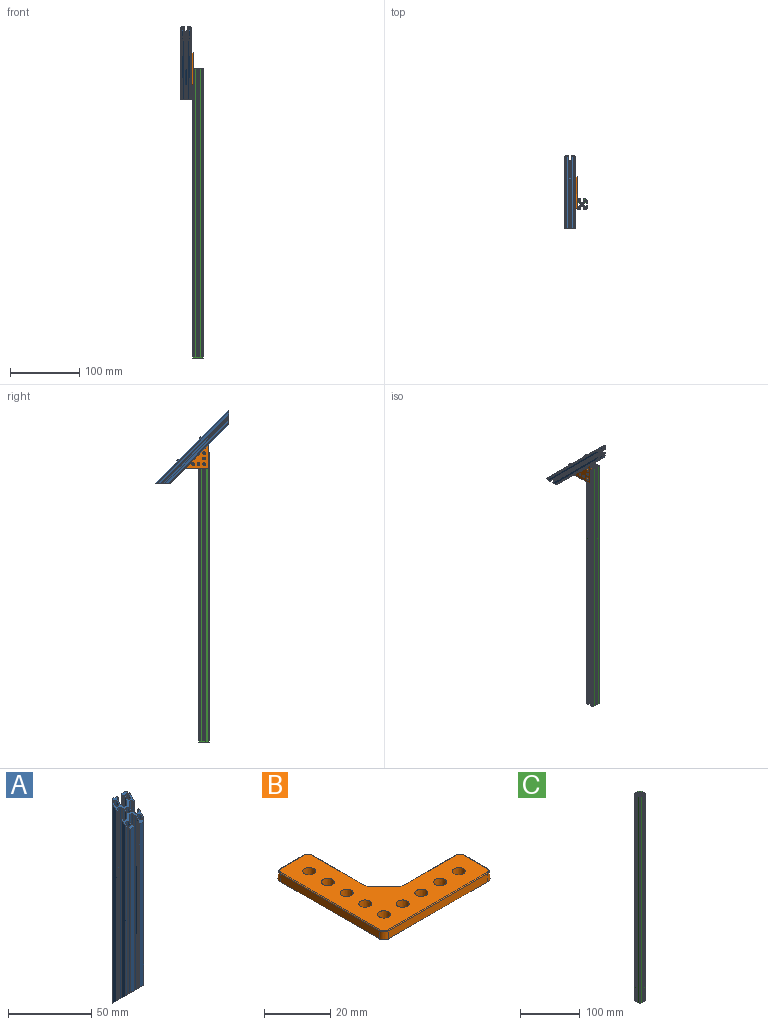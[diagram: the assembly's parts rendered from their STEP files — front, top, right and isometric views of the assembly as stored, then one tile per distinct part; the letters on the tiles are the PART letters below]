
ASSEMBLY  parts=3 mates=2
PART A: 115 faces, bbox 15x15x150 mm
  f0: plane 15x15mm, normal (0,-0.71,0.71), area 128.4mm2, adj f2,f3,f4,f5,f6,f7,f8,f9
  f1: plane 15x15mm, normal (0,-0.71,-0.71), area 128.4mm2, adj f2,f3,f4,f5,f6,f7,f8,f9
  f2: cylinder r=0.5mm len=130.3mm, axis (0,0,1), area 101.8mm2, adj f0,f1,f3,f4
  f3: plane 129.3x2.1mm, normal (0,1,0), area 271.5mm2, adj f0,f1,f2,f63
  f4: plane 130.8x0.25mm, normal (-1,0,0), area 32.6mm2, adj f0,f1,f2,f5
  f5: cylinder r=0.5mm len=131.8mm, axis (0,0,-1), area 103.2mm2, adj f0,f1,f4,f6
  f6: cylinder r=1mm len=133.8mm, axis (0,0,1), area 208.2mm2, adj f0,f1,f5,f7
  f7: plane 136.2x1.2mm, normal (-1,0,0), area 162mm2, adj f0,f1,f6,f8
  f8: cylinder r=1mm len=138.2mm, axis (0,0,1), area 215.9mm2, adj f0,f1,f7,f9
  f9: cylinder r=0.5mm len=139.2mm, axis (0,0,-1), area 108.8mm2, adj f0,f1,f8,f10
  f10: plane 139.7x0.25mm, normal (-1,0,0), area 34.9mm2, adj f0,f1,f9,f11
  f11: cylinder r=0.5mm len=140.7mm, axis (0,0,1), area 110.2mm2, adj f0,f1,f10,f12
  f12: plane 140.7x2.1mm, normal (0,-1,0), area 295.5mm2, adj f0,f1,f11,f13
  f13: cylinder r=0.2mm len=140.7mm, axis (0,0,1), area 44.2mm2, adj f0,f1,f12,f14
  f14: plane 140.3x0.4mm, normal (1,0,0), area 56mm2, adj f0,f1,f13,f15
  f15: cylinder r=0.5mm len=139.5mm, axis (0,0,-1), area 109.1mm2, adj f0,f1,f14,f16
  f16: plane 138.5x0.2mm, normal (0,-1,0), area 27.7mm2, adj f0,f1,f15,f17
  f17: cylinder r=0.5mm len=139.5mm, axis (0,0,-1), area 109.1mm2, adj f0,f1,f16,f18
  f18: plane 146.17x3.34mm, normal (-1,0,0), area 476.5mm2, adj f0,f1,f17,f19
  f19: cylinder r=0.5mm len=147.17mm, axis (0,0,-1), area 173.1mm2, adj f0,f1,f18,f20
  f20: plane 146.88x0.48mm, normal (0.71,0.71,0), area 100mm2, adj f0,f1,f19,f21
  f21: cylinder r=1.25mm len=147.51mm, axis (0,0,-1), area 987.9mm2, adj f0,f1,f20,f22
  f22: plane 148.29x0.48mm, normal (-0.71,-0.71,0), area 100.9mm2, adj f0,f1,f21,f23
  f23: cylinder r=0.5mm len=150mm, axis (0,0,1), area 175.9mm2, adj f0,f1,f22,f64
  f24: cylinder r=0.5mm len=150mm, axis (0,0,-1), area 117.5mm2, adj f0,f1,f25,f64
  f25: plane 149x0.2mm, normal (1,0,0), area 29.8mm2, adj f0,f1,f24,f26
  f26: cylinder r=0.5mm len=148.6mm, axis (0,0,-1), area 116.2mm2, adj f0,f1,f25,f27
  f27: plane 147.6x0.4mm, normal (0,-1,0), area 59mm2, adj f0,f1,f26,f28
  f28: cylinder r=0.2mm len=147.6mm, axis (0,0,1), area 46.3mm2, adj f0,f1,f27,f29
  f29: plane 147.2x2.1mm, normal (1,0,0), area 304.7mm2, adj f0,f1,f28,f30
  f30: cylinder r=0.5mm len=143mm, axis (0,0,1), area 111.8mm2, adj f0,f1,f29,f31
  f31: plane 142x0.25mm, normal (0,1,0), area 35.5mm2, adj f0,f1,f30,f32
  f32: cylinder r=0.5mm len=142mm, axis (0,0,-1), area 111.2mm2, adj f0,f1,f31,f33
  f33: cylinder r=1mm len=141mm, axis (0,0,1), area 219.5mm2, adj f0,f1,f32,f34
  f34: plane 139x1.2mm, normal (0,1,0), area 166.8mm2, adj f0,f1,f33,f35
  f35: cylinder r=1mm len=141mm, axis (0,0,1), area 219.5mm2, adj f0,f1,f34,f36
  f36: cylinder r=0.5mm len=142mm, axis (0,0,-1), area 111.2mm2, adj f0,f1,f35,f37
  f37: plane 142x0.25mm, normal (0,1,0), area 35.5mm2, adj f0,f1,f36,f38
  f38: cylinder r=0.5mm len=143mm, axis (0,0,1), area 111.8mm2, adj f0,f1,f37,f39
  f39: plane 147.2x2.1mm, normal (-1,0,0), area 304.7mm2, adj f0,f1,f38,f40
  f40: cylinder r=0.2mm len=147.6mm, axis (0,0,1), area 46.3mm2, adj f0,f1,f39,f41
  f41: plane 147.6x0.4mm, normal (0,-1,0), area 59mm2, adj f0,f1,f40,f42
  f42: cylinder r=0.5mm len=148.6mm, axis (0,0,-1), area 116.2mm2, adj f0,f1,f41,f44
  f43: cylinder r=0.5mm len=131.5mm, axis (0,0,-1), area 103mm2, adj f0,f1,f45,f71
  f44: plane 149x0.2mm, normal (-1,0,0), area 29.8mm2, adj f0,f1,f42,f46
  f45: plane 131.5x0.2mm, normal (0,1,0), area 26.3mm2, adj f0,f1,f43,f47
  f46: cylinder r=0.5mm len=150mm, axis (0,0,-1), area 117.5mm2, adj f0,f1,f44,f65
  f47: cylinder r=0.5mm len=131.5mm, axis (0,0,-1), area 103mm2, adj f0,f1,f45,f48
  f48: plane 130.5x0.4mm, normal (-1,0,0), area 52mm2, adj f0,f1,f47,f50
  f49: cylinder r=0.5mm len=150mm, axis (0,0,-1), area 175.9mm2, adj f0,f1,f51,f65
  f50: cylinder r=0.2mm len=129.7mm, axis (0,0,1), area 40.7mm2, adj f0,f1,f48,f86
  f51: plane 148.29x0.48mm, normal (0.71,-0.71,0), area 100.9mm2, adj f0,f1,f49,f52
  f52: cylinder r=1.25mm len=147.51mm, axis (0,0,-1), area 987.9mm2, adj f0,f1,f51,f53
  f53: plane 146.88x0.48mm, normal (-0.71,0.71,0), area 100mm2, adj f0,f1,f52,f54
  f54: cylinder r=0.5mm len=147.17mm, axis (0,0,1), area 173.1mm2, adj f0,f1,f53,f55
  f55: plane 146.17x3.34mm, normal (1,0,0), area 476.5mm2, adj f0,f1,f54,f94
  f56: plane 124.09x0.48mm, normal (0.71,-0.71,0), area 84.4mm2, adj f0,f1,f57,f68
  f57: cylinder r=0.5mm len=123.83mm, axis (0,0,1), area 145mm2, adj f0,f1,f56,f58
  f58: plane 130.5x3.34mm, normal (-1,0,0), area 424.2mm2, adj f0,f1,f57,f59
  f59: cylinder r=0.5mm len=131.5mm, axis (0,0,-1), area 103mm2, adj f0,f1,f58,f60
  f60: plane 131.5x0.2mm, normal (0,1,0), area 26.3mm2, adj f0,f1,f59,f61
  f61: cylinder r=0.5mm len=131.5mm, axis (0,0,-1), area 103mm2, adj f0,f1,f60,f62
  f62: plane 130.5x0.4mm, normal (1,0,0), area 52mm2, adj f0,f1,f61,f63
  f63: cylinder r=0.2mm len=129.7mm, axis (0,0,1), area 40.7mm2, adj f0,f1,f3,f62
  f64: plane 150x3.34mm, normal (0,1,0), area 500.4mm2, adj f0,f1,f23,f24
  f65: plane 150x3.34mm, normal (0,1,0), area 500.4mm2, adj f0,f1,f46,f49
  f66: cylinder r=0.5mm len=121.71mm, axis (0,0,-1), area 142.2mm2, adj f0,f1,f72,f90
  f67: cylinder r=0.5mm len=121.71mm, axis (0,0,1), area 142.2mm2, adj f0,f1,f73,f112
  f68: cylinder r=1.25mm len=127.52mm, axis (0,0,-1), area 854.9mm2, adj f0,f1,f56,f90
  f69: cylinder r=1.25mm len=127.52mm, axis (0,0,-1), area 854.9mm2, adj f0,f1,f112,f113
  f70: cylinder r=1.25mm len=137.5mm, axis (0,0,1), area 1060.3mm2, adj f0,f1
  f71: plane 130.5x3.34mm, normal (1,0,0), area 424.2mm2, adj f0,f1,f43,f114
  f72: plane 120x3.34mm, normal (0,-1,0), area 400.3mm2, adj f0,f1,f66,f100
  f73: plane 120x3.34mm, normal (0,-1,0), area 400.3mm2, adj f0,f1,f67,f96
  f74: plane 128x0.25mm, normal (0,-1,0), area 32mm2, adj f0,f1,f92,f102
  f75: plane 131x1.2mm, normal (0,-1,0), area 157.2mm2, adj f0,f1,f105,f106
  f76: plane 128x0.25mm, normal (0,-1,0), area 32mm2, adj f0,f1,f98,f101
  f77: plane 127x2.1mm, normal (1,0,0), area 262.3mm2, adj f0,f1,f98,f109
  f78: plane 122.4x0.4mm, normal (0,1,0), area 49mm2, adj f0,f1,f99,f109
  f79: plane 121.4x0.2mm, normal (1,0,0), area 24.2mm2, adj f0,f1,f99,f100
  f80: plane 121.4x0.2mm, normal (-1,0,0), area 24.2mm2, adj f0,f1,f96,f97
  f81: plane 122.4x0.4mm, normal (0,1,0), area 49mm2, adj f0,f1,f97,f110
  f82: plane 127x2.1mm, normal (-1,0,0), area 262.3mm2, adj f0,f1,f92,f110
  f83: plane 139.7x0.25mm, normal (1,0,0), area 34.9mm2, adj f0,f1,f91,f103
  f84: plane 136.2x1.2mm, normal (1,0,0), area 162mm2, adj f0,f1,f107,f108
  f85: plane 130.8x0.25mm, normal (1,0,0), area 32.6mm2, adj f0,f1,f95,f104
  f86: plane 129.3x2.1mm, normal (0,1,0), area 271.5mm2, adj f0,f1,f50,f95
  f87: plane 138.5x0.2mm, normal (0,-1,0), area 27.7mm2, adj f0,f1,f93,f94
  f88: plane 140.3x0.4mm, normal (-1,0,0), area 56mm2, adj f0,f1,f93,f111
  f89: plane 140.7x2.1mm, normal (0,-1,0), area 295.5mm2, adj f0,f1,f91,f111
  f90: plane 122.67x0.48mm, normal (-0.71,0.71,0), area 83.4mm2, adj f0,f1,f66,f68
  f91: cylinder r=0.5mm len=140.7mm, axis (0,0,1), area 110.2mm2, adj f0,f1,f83,f89
  f92: cylinder r=0.5mm len=128mm, axis (0,0,1), area 100.2mm2, adj f0,f1,f74,f82
  f93: cylinder r=0.5mm len=139.5mm, axis (0,0,-1), area 109.1mm2, adj f0,f1,f87,f88
  f94: cylinder r=0.5mm len=139.5mm, axis (0,0,-1), area 109.1mm2, adj f0,f1,f55,f87
  f95: cylinder r=0.5mm len=130.3mm, axis (0,0,1), area 101.8mm2, adj f0,f1,f85,f86
  f96: cylinder r=0.5mm len=121mm, axis (0,0,-1), area 94.5mm2, adj f0,f1,f73,f80
  f97: cylinder r=0.5mm len=122.4mm, axis (0,0,-1), area 95.8mm2, adj f0,f1,f80,f81
  f98: cylinder r=0.5mm len=128mm, axis (0,0,1), area 100.2mm2, adj f0,f1,f76,f77
  f99: cylinder r=0.5mm len=122.4mm, axis (0,0,-1), area 95.8mm2, adj f0,f1,f78,f79
  f100: cylinder r=0.5mm len=121mm, axis (0,0,-1), area 94.5mm2, adj f0,f1,f72,f79
  f101: cylinder r=0.5mm len=129mm, axis (0,0,-1), area 100.8mm2, adj f0,f1,f76,f105
  f102: cylinder r=0.5mm len=129mm, axis (0,0,-1), area 100.8mm2, adj f0,f1,f74,f106
  f103: cylinder r=0.5mm len=139.2mm, axis (0,0,-1), area 108.8mm2, adj f0,f1,f83,f107
  f104: cylinder r=0.5mm len=131.8mm, axis (0,0,-1), area 103.2mm2, adj f0,f1,f85,f108
  f105: cylinder r=1mm len=131mm, axis (0,0,1), area 204.6mm2, adj f0,f1,f75,f101
  f106: cylinder r=1mm len=131mm, axis (0,0,1), area 204.6mm2, adj f0,f1,f75,f102
  f107: cylinder r=1mm len=138.2mm, axis (0,0,1), area 215.9mm2, adj f0,f1,f84,f103
  f108: cylinder r=1mm len=133.8mm, axis (0,0,1), area 208.2mm2, adj f0,f1,f84,f104
  f109: cylinder r=0.2mm len=122.8mm, axis (0,0,1), area 38.5mm2, adj f0,f1,f77,f78
  f110: cylinder r=0.2mm len=122.8mm, axis (0,0,1), area 38.5mm2, adj f0,f1,f81,f82
  f111: cylinder r=0.2mm len=140.7mm, axis (0,0,1), area 44.2mm2, adj f0,f1,f88,f89
  f112: plane 122.67x0.48mm, normal (0.71,0.71,0), area 83.4mm2, adj f0,f1,f67,f69
  f113: plane 124.09x0.48mm, normal (-0.71,-0.71,0), area 84.4mm2, adj f0,f1,f69,f114
  f114: cylinder r=0.5mm len=123.83mm, axis (0,0,-1), area 145mm2, adj f0,f1,f71,f113
PART B: 143 faces, bbox 46.6x46.6x4.1 mm
  f0: torus R=2.02mm, axis (0,0,-1), area 0.2mm2, adj f11,f80,f130,f131
  f1: torus R=2.02mm, axis (0,0,-1), area 0.2mm2, adj f12,f84,f133,f134
  f2: cone r=1.96mm half-angle=5deg, axis (0,0,1), area 34.6mm2, adj f13,f62
  f3: cone r=1.96mm half-angle=5deg, axis (0,0,1), area 34.6mm2, adj f13,f62
  f4: cone r=1.96mm half-angle=5deg, axis (0,0,1), area 34.6mm2, adj f13,f62
  f5: cone r=1.96mm half-angle=5deg, axis (0,0,1), area 34.6mm2, adj f11,f13,f62,f79
  f6: cone r=1.96mm half-angle=5deg, axis (0,0,1), area 34.6mm2, adj f12,f13,f62,f83
  f7: cone r=1.96mm half-angle=5deg, axis (0,0,1), area 34.6mm2, adj f13,f62,f87
  f8: cone r=1.96mm half-angle=5deg, axis (0,0,1), area 34.6mm2, adj f13,f62,f105,f106
  f9: cone r=1.96mm half-angle=5deg, axis (0,0,1), area 34.6mm2, adj f13,f62,f110,f111
  f10: cone r=1.96mm half-angle=5deg, axis (0,0,1), area 34.6mm2, adj f13,f62,f115
  f11: cone r=1.77mm half-angle=5deg, axis (0,0,-1), area 0.7mm2, adj f0,f5,f26,f37,f130
  f12: cone r=1.77mm half-angle=5deg, axis (0,0,-1), area 0.7mm2, adj f1,f6,f29,f34,f133
  f13: plane 46.61x46.61mm, normal (0,0,-1), area 948.9mm2, adj f2,f3,f4,f5,f6,f7,f8,f9
  f14: plane 3.9x0.77mm, normal (1,0,-0.09), area 3mm2, adj f13,f15,f61,f63
  f15: cylinder r=1mm len=1.06mm, axis (-0.09,-0.09,-0.99), area 1.2mm2, adj f13,f14,f64,f65
  f16: plane 10x2.77mm, normal (0,1,0.09), area 27.8mm2, adj f13,f17,f45,f64,f66
  f17: cone r=2mm half-angle=5deg, axis (0,0,-1), area 8.2mm2, adj f13,f16,f18,f67
  f18: plane 22.17x2.77mm, normal (1,0,0.09), area 61.7mm2, adj f13,f17,f68,f69
  f19: plane 6.5x6.5mm, normal (0.7,0.7,0.09), area 24.9mm2, adj f13,f68,f70,f71
  f20: plane 22.17x2.77mm, normal (0,1,0.09), area 61.7mm2, adj f13,f21,f70,f72
  f21: cone r=2mm half-angle=5deg, axis (0,0,-1), area 8.2mm2, adj f13,f20,f22,f73
  f22: plane 10x2.77mm, normal (1,0,0.09), area 27.8mm2, adj f13,f21,f41,f74,f75
  f23: cylinder r=1mm len=1.06mm, axis (-0.09,-0.09,-0.99), area 1.2mm2, adj f13,f24,f74,f76
  f24: plane 3.9x0.77mm, normal (0,1,-0.09), area 3mm2, adj f13,f23,f25,f77
  f25: bspline ~1.3x1.12mm, area 1.4mm2, adj f13,f24,f78,f79
  f26: bspline ~1.3x1.1mm, area 1.4mm2, adj f11,f13,f27,f80
  f27: plane 2.8x0.77mm, normal (0,1,-0.09), area 2.1mm2, adj f13,f26,f28,f81
  f28: bspline ~1.3x1.12mm, area 1.4mm2, adj f13,f27,f82,f83
  f29: bspline ~1.3x1.1mm, area 1.4mm2, adj f12,f13,f30,f84
  f30: plane 2.8x0.77mm, normal (0,1,-0.09), area 2.1mm2, adj f13,f29,f31,f85
  f31: bspline ~1.3x1.12mm, area 1.4mm2, adj f13,f30,f86,f87
  f32: bspline ~1.3x1.1mm, area 1.4mm2, adj f13,f33,f87,f88
  f33: plane 2.8x0.77mm, normal (0,-1,-0.09), area 2.1mm2, adj f13,f32,f34,f89
  f34: bspline ~1.3x1.12mm, area 1.4mm2, adj f12,f13,f33,f90
  f35: bspline ~1.3x1.1mm, area 1.4mm2, adj f13,f36,f83,f91
  f36: plane 2.8x0.77mm, normal (0,-1,-0.09), area 2.1mm2, adj f13,f35,f37,f92
  f37: bspline ~1.3x1.12mm, area 1.4mm2, adj f11,f13,f36,f93
  f38: bspline ~1.3x1.1mm, area 1.4mm2, adj f13,f39,f79,f94
  f39: plane 3.9x0.77mm, normal (0,-1,-0.09), area 3mm2, adj f13,f38,f40,f95
  f40: cylinder r=1mm len=1.06mm, axis (-0.09,0.09,-0.99), area 1.2mm2, adj f13,f39,f74,f96
  f41: cone r=2mm half-angle=5deg, axis (0,0,-1), area 8.2mm2, adj f13,f22,f42,f97
  f42: plane 42.5x2.77mm, normal (0,-1,0.09), area 118.3mm2, adj f13,f41,f43,f98
  f43: cone r=2mm half-angle=5deg, axis (0,0,-1), area 8.2mm2, adj f13,f42,f44,f99
  f44: plane 42.5x2.77mm, normal (-1,0,0.09), area 118.3mm2, adj f13,f43,f45,f100
  f45: cone r=2mm half-angle=5deg, axis (0,0,-1), area 8.2mm2, adj f13,f16,f44,f101
  f46: cylinder r=1mm len=1.06mm, axis (0.09,-0.09,-0.99), area 1.2mm2, adj f13,f47,f64,f102
  f47: plane 3.9x0.77mm, normal (-1,0,-0.09), area 3mm2, adj f13,f46,f48,f103
  f48: bspline ~1.3x1.12mm, area 1.4mm2, adj f13,f47,f104,f105
  f49: bspline ~1.3x1.1mm, area 1.4mm2, adj f13,f50,f106,f107
  f50: plane 2.8x0.77mm, normal (-1,0,-0.09), area 2.1mm2, adj f13,f49,f51,f108
  f51: bspline ~1.3x1.12mm, area 1.4mm2, adj f13,f50,f109,f110
  f52: bspline ~1.3x1.1mm, area 1.4mm2, adj f13,f53,f111,f112
  f53: plane 2.8x0.77mm, normal (-1,0,-0.09), area 2.1mm2, adj f13,f52,f54,f113
  f54: bspline ~1.3x1.12mm, area 1.4mm2, adj f13,f53,f114,f115
  f55: bspline ~1.3x1.1mm, area 1.4mm2, adj f13,f56,f115,f116
  f56: plane 2.8x0.77mm, normal (1,0,-0.09), area 2.1mm2, adj f13,f55,f57,f117
  f57: bspline ~1.3x1.12mm, area 1.4mm2, adj f13,f56,f111,f118
  f58: bspline ~1.3x1.1mm, area 1.4mm2, adj f13,f59,f110,f119
  f59: plane 2.8x0.77mm, normal (1,0,-0.09), area 2.1mm2, adj f13,f58,f60,f120
  f60: bspline ~1.3x1.12mm, area 1.4mm2, adj f13,f59,f106,f121
  f61: bspline ~1.3x1.1mm, area 1.4mm2, adj f13,f14,f105,f122
  f62: plane 45.52x45.52mm, normal (0,0,1), area 934.8mm2, adj f2,f3,f4,f5,f6,f7,f8,f9
  f63: cylinder r=0.25mm len=3.75mm, axis (0,1,0), area 1.4mm2, adj f14,f65,f122,f125
  f64: plane 1.41x0.77mm, normal (0,1,-0.09), area 1mm2, adj f15,f16,f46,f126
  f65: bspline ~1x1mm, area 0.5mm2, adj f15,f63,f125,f126
  f66: cylinder r=0.25mm len=10mm, axis (-1,0,0), area 3.7mm2, adj f16,f62,f67,f101
  f67: torus R=1.51mm, axis (0,0,-1), area 1mm2, adj f17,f62,f66,f69
  f68: cone r=2.24mm half-angle=5deg, axis (0,0,1), area 4.6mm2, adj f13,f18,f19,f123
  f69: cylinder r=0.25mm len=22.17mm, axis (0,1,0), area 8.2mm2, adj f18,f62,f67,f123
  f70: cone r=2.24mm half-angle=5deg, axis (0,0,1), area 4.6mm2, adj f13,f19,f20,f124
  f71: cylinder r=0.25mm len=6.5mm, axis (0.71,-0.71,0), area 3.3mm2, adj f19,f62,f123,f124
  f72: cylinder r=0.25mm len=22.17mm, axis (-1,0,0), area 8.2mm2, adj f20,f62,f73,f124
  f73: torus R=1.51mm, axis (0,0,-1), area 1mm2, adj f21,f62,f72,f75
  f74: plane 1.41x0.77mm, normal (1,0,-0.09), area 1mm2, adj f22,f23,f40,f127
  f75: cylinder r=0.25mm len=10mm, axis (0,1,0), area 3.7mm2, adj f22,f62,f73,f97
  f76: bspline ~1x1mm, area 0.5mm2, adj f23,f77,f127,f128
  f77: cylinder r=0.25mm len=3.75mm, axis (-1,0,0), area 1.4mm2, adj f24,f76,f78,f128
  f78: bspline ~1.23x1.01mm, area 0.6mm2, adj f25,f77,f128,f129
  f79: cone r=1.77mm half-angle=5deg, axis (0,0,-1), area 0.7mm2, adj f5,f25,f38,f129
  f80: bspline ~1.23x1.01mm, area 0.6mm2, adj f0,f26,f81,f131
  f81: cylinder r=0.25mm len=2.62mm, axis (-1,0,0), area 1mm2, adj f27,f80,f82,f131
  f82: bspline ~1.23x1.01mm, area 0.6mm2, adj f28,f81,f131,f132
  f83: cone r=1.77mm half-angle=5deg, axis (0,0,-1), area 0.7mm2, adj f6,f28,f35,f132
  f84: bspline ~1.23x1.03mm, area 0.6mm2, adj f1,f29,f85,f134
  f85: cylinder r=0.25mm len=2.62mm, axis (-1,0,0), area 1mm2, adj f30,f84,f86,f134
  f86: bspline ~1.23x1.01mm, area 0.6mm2, adj f31,f85,f134,f135
  f87: cone r=1.77mm half-angle=5deg, axis (0,0,-1), area 0.7mm2, adj f7,f31,f32,f135
  f88: bspline ~1.23x1.01mm, area 0.6mm2, adj f32,f89,f134,f135
  f89: cylinder r=0.25mm len=2.62mm, axis (1,0,0), area 1mm2, adj f33,f88,f90,f134
  f90: bspline ~1.23x1.03mm, area 0.6mm2, adj f34,f89,f133,f134
  f91: bspline ~1.23x1.03mm, area 0.6mm2, adj f35,f92,f131,f132
  f92: cylinder r=0.25mm len=2.62mm, axis (1,0,0), area 1mm2, adj f36,f91,f93,f131
  f93: bspline ~1.23x1.01mm, area 0.6mm2, adj f37,f92,f130,f131
  f94: bspline ~1.23x1.03mm, area 0.6mm2, adj f38,f95,f128,f129
  f95: cylinder r=0.25mm len=3.75mm, axis (1,0,0), area 1.4mm2, adj f39,f94,f96,f128
  f96: bspline ~1x1mm, area 0.5mm2, adj f40,f95,f127,f128
  f97: torus R=1.51mm, axis (0,0,-1), area 1mm2, adj f41,f62,f75,f98
  f98: cylinder r=0.25mm len=42.5mm, axis (1,0,0), area 15.8mm2, adj f42,f62,f97,f99
  f99: torus R=1.51mm, axis (0,0,-1), area 1mm2, adj f43,f62,f98,f100
  f100: cylinder r=0.25mm len=42.5mm, axis (0,-1,0), area 15.8mm2, adj f44,f62,f99,f101
  f101: torus R=1.51mm, axis (0,0,-1), area 1mm2, adj f45,f62,f66,f100
  f102: bspline ~1x1mm, area 0.5mm2, adj f46,f103,f125,f126
  f103: cylinder r=0.25mm len=3.75mm, axis (0,-1,0), area 1.4mm2, adj f47,f102,f104,f125
  f104: bspline ~1.23x1.01mm, area 0.6mm2, adj f48,f103,f125,f136
  f105: cone r=1.77mm half-angle=5deg, axis (0,0,-1), area 0.7mm2, adj f8,f48,f61,f136
  f106: cone r=1.77mm half-angle=5deg, axis (0,0,-1), area 0.7mm2, adj f8,f49,f60,f137
  f107: bspline ~1.23x1.01mm, area 0.6mm2, adj f49,f108,f137,f138
  f108: cylinder r=0.25mm len=2.62mm, axis (0,-1,0), area 1mm2, adj f50,f107,f109,f138
  f109: bspline ~1.23x1.01mm, area 0.6mm2, adj f51,f108,f138,f139
  f110: cone r=1.77mm half-angle=5deg, axis (0,0,-1), area 0.7mm2, adj f9,f51,f58,f139
  f111: cone r=1.77mm half-angle=5deg, axis (0,0,-1), area 0.7mm2, adj f9,f52,f57,f140
  f112: bspline ~1.23x1.03mm, area 0.6mm2, adj f52,f113,f140,f141
  f113: cylinder r=0.25mm len=2.62mm, axis (0,-1,0), area 1mm2, adj f53,f112,f114,f141
  f114: bspline ~1.23x1.03mm, area 0.6mm2, adj f54,f113,f141,f142
  f115: cone r=1.77mm half-angle=5deg, axis (0,0,-1), area 0.7mm2, adj f10,f54,f55,f142
  f116: bspline ~1.23x1.03mm, area 0.6mm2, adj f55,f117,f141,f142
  f117: cylinder r=0.25mm len=2.62mm, axis (0,1,0), area 1mm2, adj f56,f116,f118,f141
  f118: bspline ~1.23x1.01mm, area 0.6mm2, adj f57,f117,f140,f141
  f119: bspline ~1.23x1.03mm, area 0.6mm2, adj f58,f120,f138,f139
  f120: cylinder r=0.25mm len=2.62mm, axis (0,1,0), area 1mm2, adj f59,f119,f121,f138
  f121: bspline ~1.23x1.03mm, area 0.6mm2, adj f60,f120,f137,f138
  f122: bspline ~1.23x1.03mm, area 0.6mm2, adj f61,f63,f125,f136
  f123: torus R=2.49mm, axis (0,0,1), area 0.7mm2, adj f62,f68,f69,f71
  f124: torus R=2.49mm, axis (0,0,1), area 0.7mm2, adj f62,f70,f71,f72
  f125: plane 5.27x2.79mm, normal (0,0,-1), area 14mm2, adj f63,f65,f102,f103,f104,f122,f126,f136
  f126: cylinder r=0.25mm len=1.27mm, axis (-1,0,0), area 0.5mm2, adj f64,f65,f102,f125
  f127: cylinder r=0.25mm len=1.27mm, axis (0,1,0), area 0.5mm2, adj f74,f76,f96,f128
  f128: plane 5.27x2.79mm, normal (0,0,-1), area 14mm2, adj f76,f77,f78,f94,f95,f96,f127,f129
  f129: torus R=2.02mm, axis (0,0,-1), area 0.3mm2, adj f78,f79,f94,f128
  f130: torus R=2.02mm, axis (0,0,-1), area 0.2mm2, adj f0,f11,f93,f131
  f131: plane 4.13x2.77mm, normal (0,0,-1), area 10.8mm2, adj f0,f80,f81,f82,f91,f92,f93,f130
  f132: torus R=2.02mm, axis (0,0,-1), area 0.3mm2, adj f82,f83,f91,f131
  f133: torus R=2.02mm, axis (0,0,-1), area 0.2mm2, adj f1,f12,f90,f134
  f134: plane 4.13x2.77mm, normal (0,0,-1), area 10.8mm2, adj f1,f84,f85,f86,f88,f89,f90,f133
  f135: torus R=2.02mm, axis (0,0,-1), area 0.3mm2, adj f86,f87,f88,f134
  f136: torus R=2.02mm, axis (0,0,-1), area 0.3mm2, adj f104,f105,f122,f125
  f137: torus R=2.02mm, axis (0,0,-1), area 0.3mm2, adj f106,f107,f121,f138
  f138: plane 4.13x2.77mm, normal (0,0,-1), area 10.8mm2, adj f107,f108,f109,f119,f120,f121,f137,f139
  f139: torus R=2.02mm, axis (0,0,-1), area 0.3mm2, adj f109,f110,f119,f138
  f140: torus R=2.02mm, axis (0,0,-1), area 0.3mm2, adj f111,f112,f118,f141
  f141: plane 4.13x2.77mm, normal (0,0,-1), area 10.8mm2, adj f112,f113,f114,f116,f117,f118,f140,f142
  f142: torus R=2.02mm, axis (0,0,-1), area 0.3mm2, adj f114,f115,f116,f141
PART C: 115 faces, bbox 15x15x420 mm
  f0: plane 15x15mm, normal (0,0,1), area 90.8mm2, adj f1,f2,f3,f4,f5,f6,f7,f8
  f1: plane 420x0.48mm, normal (0.71,-0.71,0), area 286.8mm2, adj f0,f2,f59,f62
  f2: cylinder r=0.5mm len=420mm, axis (0,0,1), area 494.8mm2, adj f0,f1,f3,f62
  f3: plane 420x3.34mm, normal (-1,0,0), area 1401mm2, adj f0,f2,f4,f62
  f4: cylinder r=0.5mm len=420mm, axis (0,0,-1), area 329.9mm2, adj f0,f3,f5,f62
  f5: plane 420x0.2mm, normal (0,1,0), area 84mm2, adj f0,f4,f6,f62
  f6: cylinder r=0.5mm len=420mm, axis (0,0,-1), area 329.9mm2, adj f0,f5,f7,f62
  f7: plane 420x0.4mm, normal (1,0,0), area 168mm2, adj f0,f6,f8,f62
  f8: cylinder r=0.2mm len=420mm, axis (0,0,1), area 131.9mm2, adj f0,f7,f9,f62
  f9: plane 420x2.1mm, normal (0,1,0), area 882mm2, adj f0,f8,f10,f62
  f10: cylinder r=0.5mm len=420mm, axis (0,0,1), area 329.9mm2, adj f0,f9,f11,f62
  f11: plane 420x0.25mm, normal (-1,0,0), area 105mm2, adj f0,f10,f12,f62
  f12: cylinder r=0.5mm len=420mm, axis (0,0,-1), area 329.9mm2, adj f0,f11,f13,f62
  f13: cylinder r=1mm len=420mm, axis (0,0,1), area 659.7mm2, adj f0,f12,f14,f62
  f14: plane 420x1.2mm, normal (-1,0,0), area 504mm2, adj f0,f13,f15,f62
  f15: cylinder r=1mm len=420mm, axis (0,0,1), area 659.7mm2, adj f0,f14,f16,f62
  f16: cylinder r=0.5mm len=420mm, axis (0,0,-1), area 329.9mm2, adj f0,f15,f17,f62
  f17: plane 420x0.25mm, normal (-1,0,0), area 105mm2, adj f0,f16,f18,f62
  f18: cylinder r=0.5mm len=420mm, axis (0,0,1), area 329.9mm2, adj f0,f17,f19,f62
  f19: plane 420x2.1mm, normal (0,-1,0), area 882mm2, adj f0,f18,f20,f62
  f20: cylinder r=0.2mm len=420mm, axis (0,0,1), area 131.9mm2, adj f0,f19,f21,f62
  f21: plane 420x0.4mm, normal (1,0,0), area 168mm2, adj f0,f20,f22,f62
  f22: cylinder r=0.5mm len=420mm, axis (0,0,-1), area 329.9mm2, adj f0,f21,f23,f62
  f23: plane 420x0.2mm, normal (0,-1,0), area 84mm2, adj f0,f22,f24,f62
  f24: cylinder r=0.5mm len=420mm, axis (0,0,-1), area 329.9mm2, adj f0,f23,f25,f62
  f25: plane 420x3.34mm, normal (-1,0,0), area 1401mm2, adj f0,f24,f26,f62
  f26: cylinder r=0.5mm len=420mm, axis (0,0,-1), area 494.8mm2, adj f0,f25,f27,f62
  f27: plane 420x0.48mm, normal (0.71,0.71,0), area 286.8mm2, adj f0,f26,f28,f62
  f28: cylinder r=1.25mm len=420mm, axis (0,0,-1), area 2866.6mm2, adj f0,f27,f29,f62
  f29: plane 420x0.48mm, normal (-0.71,-0.71,0), area 286.8mm2, adj f0,f28,f30,f62
  f30: cylinder r=0.5mm len=420mm, axis (0,0,1), area 494.8mm2, adj f0,f29,f31,f62
  f31: plane 420x3.34mm, normal (0,1,0), area 1401mm2, adj f0,f30,f32,f62
  f32: cylinder r=0.5mm len=420mm, axis (0,0,-1), area 329.9mm2, adj f0,f31,f33,f62
  f33: plane 420x0.2mm, normal (1,0,0), area 84mm2, adj f0,f32,f34,f62
  f34: cylinder r=0.5mm len=420mm, axis (0,0,-1), area 329.9mm2, adj f0,f33,f35,f62
  f35: plane 420x0.4mm, normal (0,-1,0), area 168mm2, adj f0,f34,f36,f62
  f36: cylinder r=0.2mm len=420mm, axis (0,0,1), area 131.9mm2, adj f0,f35,f37,f62
  f37: plane 420x2.1mm, normal (1,0,0), area 882mm2, adj f0,f36,f38,f62
  f38: cylinder r=0.5mm len=420mm, axis (0,0,1), area 329.9mm2, adj f0,f37,f39,f62
  f39: plane 420x0.25mm, normal (0,1,0), area 105mm2, adj f0,f38,f40,f62
  f40: cylinder r=0.5mm len=420mm, axis (0,0,-1), area 329.9mm2, adj f0,f39,f41,f62
  f41: cylinder r=1mm len=420mm, axis (0,0,1), area 659.7mm2, adj f0,f40,f42,f62
  f42: plane 420x1.2mm, normal (0,1,0), area 504mm2, adj f0,f41,f43,f62
  f43: cylinder r=1mm len=420mm, axis (0,0,1), area 659.7mm2, adj f0,f42,f44,f62
  f44: cylinder r=0.5mm len=420mm, axis (0,0,-1), area 329.9mm2, adj f0,f43,f45,f62
  f45: plane 420x0.25mm, normal (0,1,0), area 105mm2, adj f0,f44,f46,f62
  f46: cylinder r=0.5mm len=420mm, axis (0,0,1), area 329.9mm2, adj f0,f45,f47,f62
  f47: plane 420x2.1mm, normal (-1,0,0), area 882mm2, adj f0,f46,f48,f62
  f48: cylinder r=0.2mm len=420mm, axis (0,0,1), area 131.9mm2, adj f0,f47,f49,f62
  f49: plane 420x0.4mm, normal (0,-1,0), area 168mm2, adj f0,f48,f50,f62
  f50: cylinder r=0.5mm len=420mm, axis (0,0,-1), area 329.9mm2, adj f0,f49,f51,f62
  f51: plane 420x0.2mm, normal (-1,0,0), area 84mm2, adj f0,f50,f52,f62
  f52: cylinder r=0.5mm len=420mm, axis (0,0,-1), area 329.9mm2, adj f0,f51,f53,f62
  f53: plane 420x3.34mm, normal (0,1,0), area 1401mm2, adj f0,f52,f54,f62
  f54: cylinder r=0.5mm len=420mm, axis (0,0,-1), area 494.8mm2, adj f0,f53,f55,f62
  f55: plane 420x0.48mm, normal (0.71,-0.71,0), area 286.8mm2, adj f0,f54,f56,f62
  f56: cylinder r=1.25mm len=420mm, axis (0,0,-1), area 2866.6mm2, adj f0,f55,f62,f112
  f57: cylinder r=0.5mm len=420mm, axis (0,0,-1), area 494.8mm2, adj f0,f62,f64,f85
  f58: cylinder r=0.5mm len=420mm, axis (0,0,1), area 494.8mm2, adj f0,f62,f65,f110
  f59: cylinder r=1.25mm len=420mm, axis (0,0,-1), area 2866.6mm2, adj f0,f1,f62,f85
  f60: cylinder r=1.25mm len=420mm, axis (0,0,-1), area 2866.6mm2, adj f0,f62,f110,f111
  f61: cylinder r=1.25mm len=420mm, axis (0,0,1), area 3298.7mm2, adj f0,f62
  f62: plane 15x15mm, normal (0,0,-1), area 90.8mm2, adj f1,f2,f3,f4,f5,f6,f7,f8
  f63: plane 420x3.34mm, normal (1,0,0), area 1401mm2, adj f0,f62,f90,f114
  f64: plane 420x3.34mm, normal (0,-1,0), area 1401mm2, adj f0,f57,f62,f97
  f65: plane 420x3.34mm, normal (0,-1,0), area 1401mm2, adj f0,f58,f62,f93
  f66: plane 420x3.34mm, normal (1,0,0), area 1401mm2, adj f0,f62,f89,f113
  f67: plane 420x0.25mm, normal (0,-1,0), area 105mm2, adj f0,f62,f87,f99
  f68: plane 420x1.2mm, normal (0,-1,0), area 504mm2, adj f0,f62,f102,f103
  f69: plane 420x0.25mm, normal (0,-1,0), area 105mm2, adj f0,f62,f95,f98
  f70: plane 420x2.1mm, normal (1,0,0), area 882mm2, adj f0,f62,f95,f106
  f71: plane 420x0.4mm, normal (0,1,0), area 168mm2, adj f0,f62,f96,f106
  f72: plane 420x0.2mm, normal (1,0,0), area 84mm2, adj f0,f62,f96,f97
  f73: plane 420x0.2mm, normal (-1,0,0), area 84mm2, adj f0,f62,f93,f94
  f74: plane 420x0.4mm, normal (0,1,0), area 168mm2, adj f0,f62,f94,f107
  f75: plane 420x2.1mm, normal (-1,0,0), area 882mm2, adj f0,f62,f87,f107
  f76: plane 420x0.25mm, normal (1,0,0), area 105mm2, adj f0,f62,f86,f100
  f77: plane 420x1.2mm, normal (1,0,0), area 504mm2, adj f0,f62,f104,f105
  f78: plane 420x0.25mm, normal (1,0,0), area 105mm2, adj f0,f62,f92,f101
  f79: plane 420x2.1mm, normal (0,1,0), area 882mm2, adj f0,f62,f92,f108
  f80: plane 420x0.4mm, normal (-1,0,0), area 168mm2, adj f0,f62,f91,f108
  f81: plane 420x0.2mm, normal (0,1,0), area 84mm2, adj f0,f62,f90,f91
  f82: plane 420x0.2mm, normal (0,-1,0), area 84mm2, adj f0,f62,f88,f89
  f83: plane 420x0.4mm, normal (-1,0,0), area 168mm2, adj f0,f62,f88,f109
  f84: plane 420x2.1mm, normal (0,-1,0), area 882mm2, adj f0,f62,f86,f109
  f85: plane 420x0.48mm, normal (-0.71,0.71,0), area 286.8mm2, adj f0,f57,f59,f62
  f86: cylinder r=0.5mm len=420mm, axis (0,0,1), area 329.9mm2, adj f0,f62,f76,f84
  f87: cylinder r=0.5mm len=420mm, axis (0,0,1), area 329.9mm2, adj f0,f62,f67,f75
  f88: cylinder r=0.5mm len=420mm, axis (0,0,-1), area 329.9mm2, adj f0,f62,f82,f83
  f89: cylinder r=0.5mm len=420mm, axis (0,0,-1), area 329.9mm2, adj f0,f62,f66,f82
  f90: cylinder r=0.5mm len=420mm, axis (0,0,-1), area 329.9mm2, adj f0,f62,f63,f81
  f91: cylinder r=0.5mm len=420mm, axis (0,0,-1), area 329.9mm2, adj f0,f62,f80,f81
  f92: cylinder r=0.5mm len=420mm, axis (0,0,1), area 329.9mm2, adj f0,f62,f78,f79
  f93: cylinder r=0.5mm len=420mm, axis (0,0,-1), area 329.9mm2, adj f0,f62,f65,f73
  f94: cylinder r=0.5mm len=420mm, axis (0,0,-1), area 329.9mm2, adj f0,f62,f73,f74
  f95: cylinder r=0.5mm len=420mm, axis (0,0,1), area 329.9mm2, adj f0,f62,f69,f70
  f96: cylinder r=0.5mm len=420mm, axis (0,0,-1), area 329.9mm2, adj f0,f62,f71,f72
  f97: cylinder r=0.5mm len=420mm, axis (0,0,-1), area 329.9mm2, adj f0,f62,f64,f72
  f98: cylinder r=0.5mm len=420mm, axis (0,0,-1), area 329.9mm2, adj f0,f62,f69,f102
  f99: cylinder r=0.5mm len=420mm, axis (0,0,-1), area 329.9mm2, adj f0,f62,f67,f103
  f100: cylinder r=0.5mm len=420mm, axis (0,0,-1), area 329.9mm2, adj f0,f62,f76,f104
  f101: cylinder r=0.5mm len=420mm, axis (0,0,-1), area 329.9mm2, adj f0,f62,f78,f105
  f102: cylinder r=1mm len=420mm, axis (0,0,1), area 659.7mm2, adj f0,f62,f68,f98
  f103: cylinder r=1mm len=420mm, axis (0,0,1), area 659.7mm2, adj f0,f62,f68,f99
  f104: cylinder r=1mm len=420mm, axis (0,0,1), area 659.7mm2, adj f0,f62,f77,f100
  f105: cylinder r=1mm len=420mm, axis (0,0,1), area 659.7mm2, adj f0,f62,f77,f101
  f106: cylinder r=0.2mm len=420mm, axis (0,0,1), area 131.9mm2, adj f0,f62,f70,f71
  f107: cylinder r=0.2mm len=420mm, axis (0,0,1), area 131.9mm2, adj f0,f62,f74,f75
  f108: cylinder r=0.2mm len=420mm, axis (0,0,1), area 131.9mm2, adj f0,f62,f79,f80
  f109: cylinder r=0.2mm len=420mm, axis (0,0,1), area 131.9mm2, adj f0,f62,f83,f84
  f110: plane 420x0.48mm, normal (0.71,0.71,0), area 286.8mm2, adj f0,f58,f60,f62
  f111: plane 420x0.48mm, normal (-0.71,-0.71,0), area 286.8mm2, adj f0,f60,f62,f114
  f112: plane 420x0.48mm, normal (-0.71,0.71,0), area 286.8mm2, adj f0,f56,f62,f113
  f113: cylinder r=0.5mm len=420mm, axis (0,0,1), area 494.8mm2, adj f0,f62,f66,f112
  f114: cylinder r=0.5mm len=420mm, axis (0,0,-1), area 494.8mm2, adj f0,f62,f63,f111
PLACE A rot(axis=(1,0,0),45deg) t=(-105.34,100.23,606.31)mm
PLACE B rot(axis=(0,-1,0),90deg) t=(-94.84,34.9,639.27)mm
PLACE C t=(-87.87,34.89,236.68)mm
MATE parallel C.f25 <-> B.f21  axis (-1,0,0) through (-95.37,38.81,446.68)mm
MATE planar A.f55 <-> B.f62  axis (1,0,0) through (-97.84,49.98,662.12)mm
